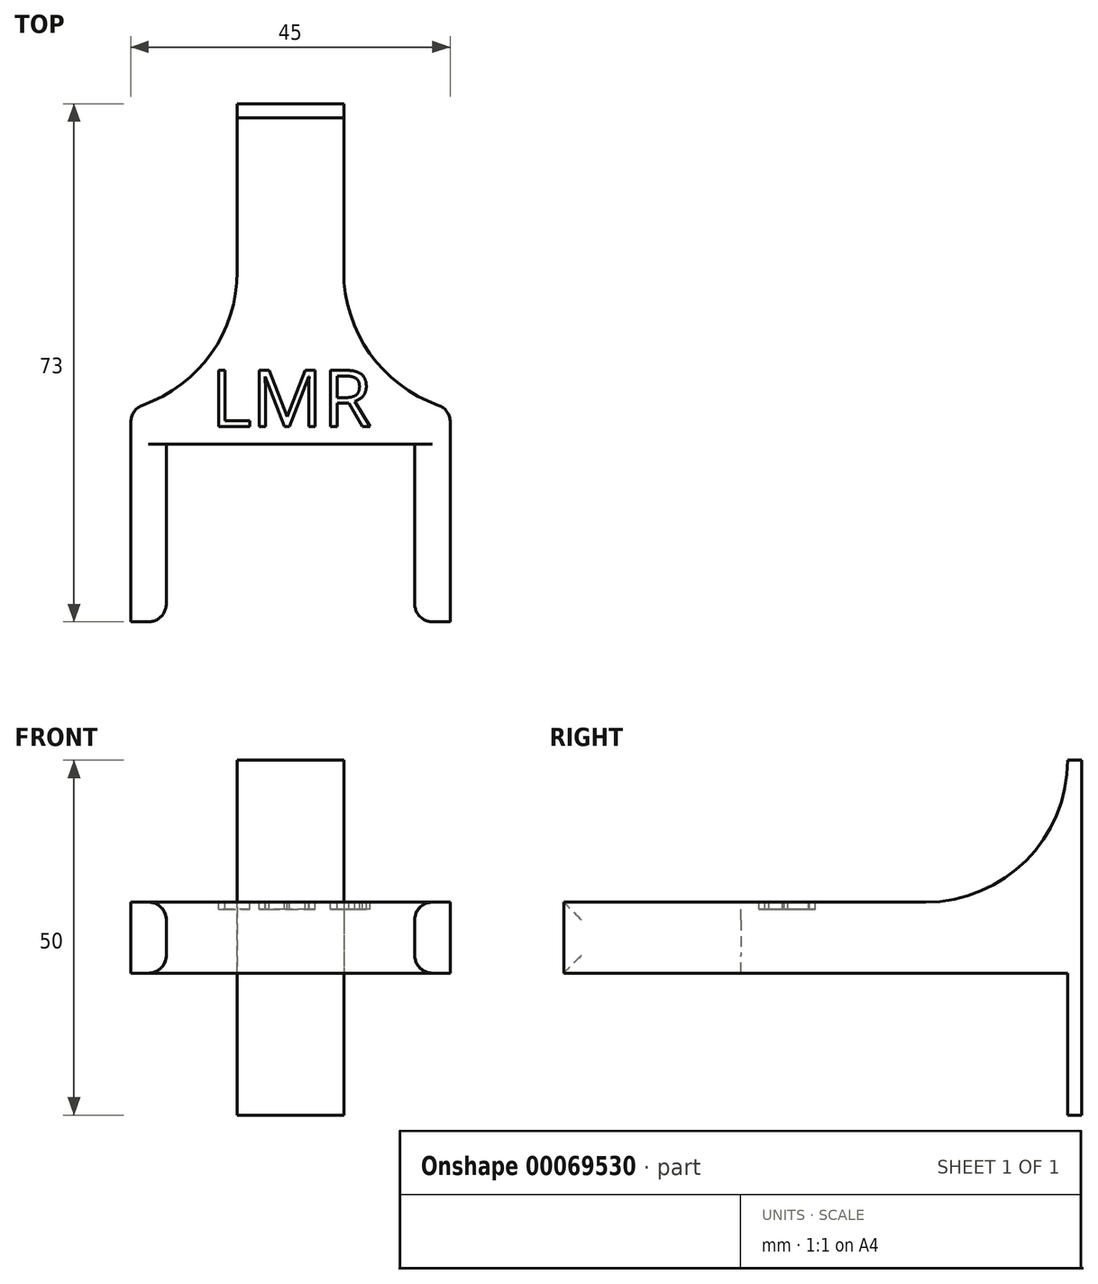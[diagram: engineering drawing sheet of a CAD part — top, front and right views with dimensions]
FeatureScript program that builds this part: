
annotation { "Feature Type Name" : "Feature", "Feature Type Description" : "" }
export const myFeature = defineFeature(function(context is Context, id is Id, definition is map)
    precondition{}
    {
        {
            var Q0;
            Q0=qCreatedBy(makeId("Top.planeOp"),FACE);
            var sketch = newSketch(context, id + "F0", { "sketchPlane" : qUnion([Q0])});
            skLineSegment(sketch, "E0.bottom", {"start": v(-17.5, -12.5) * mm, "end": v(17.5, -12.5) * mm});
            skLineSegment(sketch, "E0.top", {"start": v(-17.5, 12.5) * mm, "end": v(17.5, 12.5) * mm});
            skLineSegment(sketch, "E0.left", {"start": v(-17.5, -12.5) * mm, "end": v(-17.5, 12.5) * mm});
            skLineSegment(sketch, "E0.right", {"start": v(17.5, -12.5) * mm, "end": v(17.5, 12.5) * mm});
            skPoint(sketch, "E0.middle", {"position": v(0, 0) * mm});
            skLineSegment(sketch, "E1.bottom", {"start": v(-22.5, -12.5) * mm, "end": v(22.5, -12.5) * mm});
            skLineSegment(sketch, "E1.top", {"start": v(-22.5, 12.5) * mm, "end": v(22.5, 12.5) * mm});
            skLineSegment(sketch, "E1.left", {"start": v(-22.5, -12.5) * mm, "end": v(-22.5, 12.5) * mm});
            skLineSegment(sketch, "E1.right", {"start": v(22.5, -12.5) * mm, "end": v(22.5, 12.5) * mm});
            skLineSegment(sketch, "E2.top", {"start": v(-22.5, 17.5) * mm, "end": v(22.5, 17.5) * mm});
            skLineSegment(sketch, "E2.left", {"start": v(-22.5, 12.5) * mm, "end": v(-22.5, 17.5) * mm});
            skLineSegment(sketch, "E2.right", {"start": v(22.5, 12.5) * mm, "end": v(22.5, 17.5) * mm});
            skLineSegment(sketch, "E3", {"start": v(0, 17.5) * mm, "end": v(0, 59.5) * mm, "construction": true});
            skPoint(sketch, "E3.endSnap0", {"position": v(0, 17.5) * mm});
            skLineSegment(sketch, "E4.bottom", {"start": v(7.5, 58.5) * mm, "end": v(-7.5, 58.5) * mm});
            skLineSegment(sketch, "E4.top", {"start": v(7.5, 60.5) * mm, "end": v(-7.5, 60.5) * mm});
            skLineSegment(sketch, "E4.left", {"start": v(7.5, 58.5) * mm, "end": v(7.5, 60.5) * mm});
            skLineSegment(sketch, "E4.right", {"start": v(-7.5, 58.5) * mm, "end": v(-7.5, 60.5) * mm});
            skPoint(sketch, "E4.middle", {"position": v(0, 59.5) * mm});
            skLineSegment(sketch, "E5", {"start": v(-7.5, 58.5) * mm, "end": v(-7.5, 17.5) * mm});
            skLineSegment(sketch, "E6", {"start": v(7.5, 58.5) * mm, "end": v(7.5, 17.5) * mm});
            skSolve(sketch);
        }
        {
            var Q0;
            Q0=makeQuery(id+"F0.imprint","IMPRINT",FACE,{"disambiguationData":[TD([[makeQuery(id+"F0.imprint","IMPRINT",EDGE,{"derivedFrom":sQuery(id+"F0.wireOp",EDGE,"E4.bottom")}),1.0]])]});
            var Q1;
            {var subQ0=sQuery(id+"F0.wireOp",EDGE,"E2.left");Q1=makeQuery(id+"F0.imprint","IMPRINT",FACE,{"disambiguationData":[TD([[makeQuery(id+"F0.imprint","IMPRINT",EDGE,{"derivedFrom":subQ0}),-1.0]])]});}
            var Q2;
            {var subQ0=sQuery(id+"F0.wireOp",EDGE,"E0.right");Q2=makeQuery(id+"F0.imprint","IMPRINT",FACE,{"disambiguationData":[TD([[makeQuery(id+"F0.imprint","IMPRINT",EDGE,{"derivedFrom":subQ0}),-1.0]])]});}
            var Q3;
            {var subQ0=sQuery(id+"F0.wireOp",EDGE,"E0.left");Q3=makeQuery(id+"F0.imprint","IMPRINT",FACE,{"disambiguationData":[TD([[makeQuery(id+"F0.imprint","IMPRINT",EDGE,{"derivedFrom":subQ0}),1.0]])]});}
            extrude(context, id + "F1", {"entities" : qUnion([Q0, Q1, Q2, Q3]), "endBound" : BoundingType.SYMMETRIC, "depth" : 10 * mm});
        }
        {
            var Q0;
            Q0=makeQuery(id+"F0.imprint","IMPRINT",FACE,{"disambiguationData":[TD([[makeQuery(id+"F0.imprint","IMPRINT",EDGE,{"derivedFrom":sQuery(id+"F0.wireOp",EDGE,"E4.bottom")}),-1.0]])]});
            extrude(context, id + "F2", {"entities" : qUnion([Q0]), "operationType" : NewBodyOperationType.ADD, "endBound" : BoundingType.SYMMETRIC, "depth" : 50 * mm});
        }
        {
            var Q0;
            Q0=makeQuery(id+"F1.opExtrude","CAP_EDGE",EDGE,{"disambiguationData":[OSD([sQuery(id+"F0.wireOp",EDGE,"E4.bottom")])],"isStart":false});
            var Q1;
            Q1=makeQuery(id+"F1.opExtrude","CAP_EDGE",EDGE,{"disambiguationData":[OSD([sQuery(id+"F0.wireOp",EDGE,"E4.bottom")])],"isStart":true});
            var Q2;
            Q2=makeQuery(id+"F1.opExtrude","SWEPT_EDGE",EDGE,{"disambiguationData":[OSD([sQuery(id+"F0.wireOp",EDGE,"E2.top"),sQuery(id+"F0.wireOp",EDGE,"E6")])]});
            var Q3;
            Q3=makeQuery(id+"F1.opExtrude","SWEPT_EDGE",EDGE,{"disambiguationData":[OSD([sQuery(id+"F0.wireOp",EDGE,"E2.top"),sQuery(id+"F0.wireOp",EDGE,"E5")])]});
            fillet(context, id + "F3", {"entities" : qUnion([Q0, Q1, Q2, Q3]), "radius" : 20 * mm, "tangentPropagation" : true, "allowEdgeOverflow" : false});
        }
        {
            var Q0;
            Q0=makeQuery(id+"F1.opExtrude","SWEPT_EDGE",EDGE,{"disambiguationData":[OSD([sQuery(id+"F0.wireOp",EDGE,"E0.right"),sQuery(id+"F0.wireOp",EDGE,"E1.bottom")])]});
            var Q1;
            Q1=makeQuery(id+"F1.opExtrude","SWEPT_EDGE",EDGE,{"disambiguationData":[OSD([sQuery(id+"F0.wireOp",EDGE,"E0.left"),sQuery(id+"F0.wireOp",EDGE,"E1.bottom")])]});
            var Q2;
            Q2=makeQuery(id+"F3.opFillet","BLEND_EDGE",EDGE,{"blendedFrom":[makeQuery(id+"F1.opExtrude","SWEPT_EDGE",EDGE,{"disambiguationData":[OSD([sQuery(id+"F0.wireOp",EDGE,"E2.top"),sQuery(id+"F0.wireOp",EDGE,"E6")])]}),makeQuery(id+"F1.opExtrude","SWEPT_FACE",FACE,{"disambiguationData":[OSD([sQuery(id+"F0.wireOp",EDGE,"E1.right"),sQuery(id+"F0.wireOp",EDGE,"E2.right")])]})],"blendedInto":[makeQuery(id+"F1.opExtrude","SWEPT_FACE",FACE,{"disambiguationData":[OSD([sQuery(id+"F0.wireOp",EDGE,"E1.right"),sQuery(id+"F0.wireOp",EDGE,"E2.right")])]})]});
            var Q3;
            Q3=makeQuery(id+"F3.opFillet","BLEND_EDGE",EDGE,{"blendedFrom":[makeQuery(id+"F1.opExtrude","SWEPT_EDGE",EDGE,{"disambiguationData":[OSD([sQuery(id+"F0.wireOp",EDGE,"E2.top"),sQuery(id+"F0.wireOp",EDGE,"E5")])]}),makeQuery(id+"F1.opExtrude","SWEPT_FACE",FACE,{"disambiguationData":[OSD([sQuery(id+"F0.wireOp",EDGE,"E1.left"),sQuery(id+"F0.wireOp",EDGE,"E2.left")])]})],"blendedInto":[makeQuery(id+"F1.opExtrude","SWEPT_FACE",FACE,{"disambiguationData":[OSD([sQuery(id+"F0.wireOp",EDGE,"E1.left"),sQuery(id+"F0.wireOp",EDGE,"E2.left")])]})]});
            var Q4;
            Q4=makeQuery(id+"F1.opExtrude","CAP_EDGE",EDGE,{"disambiguationData":[OSD([sQuery(id+"F0.wireOp",EDGE,"E0.left")])],"isStart":true});
            var Q5;
            Q5=makeQuery(id+"F1.opExtrude","CAP_EDGE",EDGE,{"disambiguationData":[OSD([sQuery(id+"F0.wireOp",EDGE,"E0.left")])],"isStart":false});
            var Q6;
            Q6=makeQuery(id+"F1.opExtrude","CAP_EDGE",EDGE,{"disambiguationData":[OSD([sQuery(id+"F0.wireOp",EDGE,"E0.right")])],"isStart":true});
            var Q7;
            Q7=makeQuery(id+"F1.opExtrude","CAP_EDGE",EDGE,{"disambiguationData":[OSD([sQuery(id+"F0.wireOp",EDGE,"E0.right")])],"isStart":false});
            var Q8;
            Q8=makeQuery(id+"F1.opExtrude","CAP_EDGE",EDGE,{"disambiguationData":[OSD([sQuery(id+"F0.wireOp",EDGE,"E1.top")])],"isStart":false});
            var Q9;
            Q9=makeQuery(id+"F1.opExtrude","CAP_EDGE",EDGE,{"disambiguationData":[OSD([sQuery(id+"F0.wireOp",EDGE,"E1.top")])],"isStart":true});
            fillet(context, id + "F4", {"entities" : qUnion([Q0, Q1, Q2, Q3, Q4, Q5, Q6, Q7, Q8, Q9]), "radius" : 2.5 * mm, "tangentPropagation" : true, "allowEdgeOverflow" : false});
        }
        {
            var Q0;
            Q0=makeQuery(id+"F1.opExtrude","CAP_FACE",FACE,{"disambiguationData":[OSD([sQuery(id+"F0.wireOp",EDGE,"E0.left"),sQuery(id+"F0.wireOp",EDGE,"E0.right"),sQuery(id+"F0.wireOp",EDGE,"E1.bottom"),sQuery(id+"F0.wireOp",EDGE,"E1.left"),sQuery(id+"F0.wireOp",EDGE,"E1.right"),sQuery(id+"F0.wireOp",EDGE,"E1.top"),sQuery(id+"F0.wireOp",EDGE,"E2.top"),sQuery(id+"F0.wireOp",EDGE,"E2.left"),sQuery(id+"F0.wireOp",EDGE,"E2.right"),sQuery(id+"F0.wireOp",EDGE,"E4.bottom"),sQuery(id+"F0.wireOp",EDGE,"E5"),sQuery(id+"F0.wireOp",EDGE,"E6")])],"isStart":false});
            var sketch = newSketch(context, id + "F5", { "sketchPlane" : qUnion([Q0])});
            skText(sketch, "E7", { "text": "LMR", "fontName": "OpenSans-Regular.ttf"});
            skLineSegment(sketch, "E8", {"start": v(0, 0) * mm, "end": v(0, 59.64) * mm, "construction": true});
            skPoint(sketch, "E8.endSnap0", {"position": v(0, 38.5) * mm});
            const initialGuessF5  = {"E7": [-0.01124, 0.015, 1, 0, 0.008]};
            skSetInitialGuess(sketch, initialGuessF5);
            skSolve(sketch);
        }
        {
            var Q0;
            Q0 = qSketchRegion(id + "F5", true);
            extrude(context, id + "F6", {"entities" : qUnion([Q0]), "operationType" : NewBodyOperationType.REMOVE, "oppositeDirection" : true, "depth" : 1 * mm});
        }
    });
